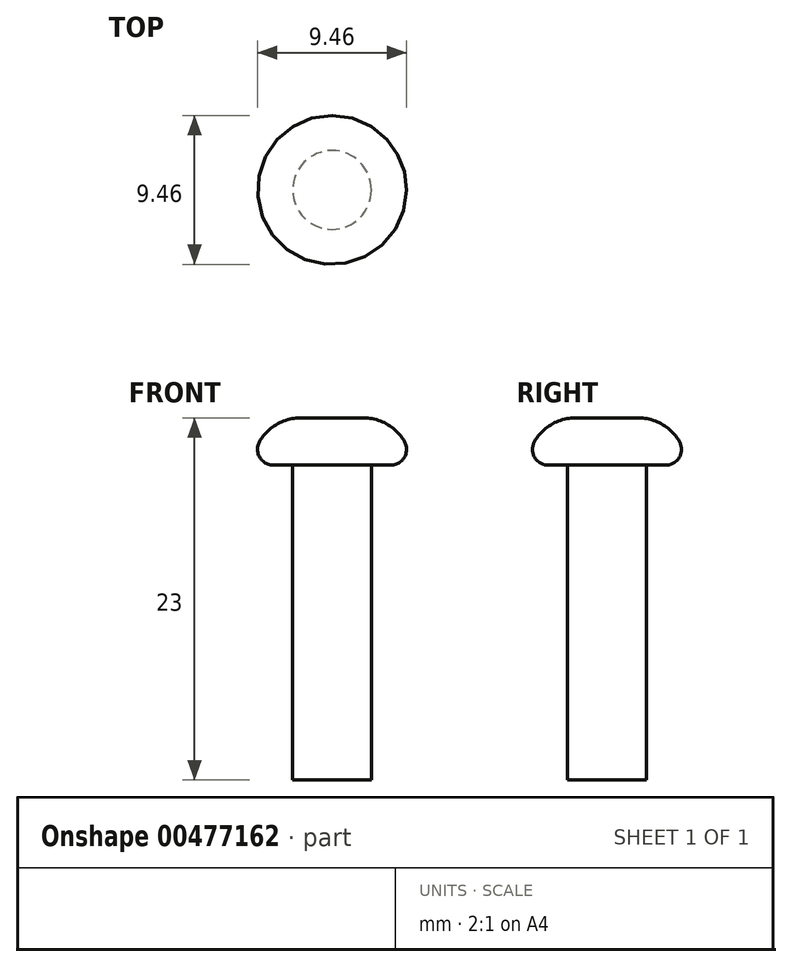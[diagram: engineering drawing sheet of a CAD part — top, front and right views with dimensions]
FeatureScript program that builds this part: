
annotation { "Feature Type Name" : "Feature", "Feature Type Description" : "" }
export const myFeature = defineFeature(function(context is Context, id is Id, definition is map)
    precondition{}
    {
        {
            var Q0;
            Q0=qCreatedBy(makeId("Top.planeOp"),FACE);
            var sketch = newSketch(context, id + "F0", { "sketchPlane" : qUnion([Q0])});
            skCircle(sketch, "E0", {"center": v(0, 0) * mm, "radius": 2.5 * mm});
            skSolve(sketch);
        }
        {
            var Q0;
            Q0=qSketchRegion(id+"F0",true);
            extrude(context, id + "F1", {"entities" : qUnion([Q0]), "oppositeDirection" : true, "depth" : 20 * mm});
        }
        {
            var Q0;
            Q0=makeQuery(id+"F1.opExtrude","CAP_FACE",FACE,{"disambiguationData":[OSD([sQuery(id+"F0.wireOp",EDGE,"E0")])],"isStart":true});
            var sketch = newSketch(context, id + "F2", { "sketchPlane" : qUnion([Q0])});
            skCircle(sketch, "E1", {"center": v(0, 0) * mm, "radius": 5 * mm});
            skSolve(sketch);
        }
        {
            var Q0;
            Q0=qSketchRegion(id+"F2",true);
            extrude(context, id + "F3", {"entities" : qUnion([Q0]), "operationType" : NewBodyOperationType.ADD, "depth" : 3 * mm});
        }
        {
            var Q0;
            Q0=makeQuery(id+"F3.opExtrude","CAP_EDGE",EDGE,{"disambiguationData":[OSD([sQuery(id+"F2.wireOp",EDGE,"E1")])],"isStart":false});
            fillet(context, id + "F4", {"entities" : qUnion([Q0]), "radius" : 3 * mm, "tangentPropagation" : true, "allowEdgeOverflow" : false});
        }
        {
            var Q0;
            {var subQ0=sQuery(id+"F2.wireOp",EDGE,"E1");Q0=makeQuery(id+"F4.opFillet","BLEND_EDGE",EDGE,{"blendedFrom":[makeQuery(id+"F3.opExtrude","CAP_EDGE",EDGE,{"disambiguationData":[OSD([subQ0])],"isStart":false}),makeQuery(id+"F3.opExtrude","CAP_FACE",FACE,{"disambiguationData":[OSD([subQ0])],"isStart":true})],"blendedInto":[makeQuery(id+"F3.opExtrude","CAP_FACE",FACE,{"disambiguationData":[OSD([subQ0])],"isStart":true})]});}
            fillet(context, id + "F5", {"entities" : qUnion([Q0]), "radius" : 1 * mm, "tangentPropagation" : true, "allowEdgeOverflow" : false});
        }
    });
